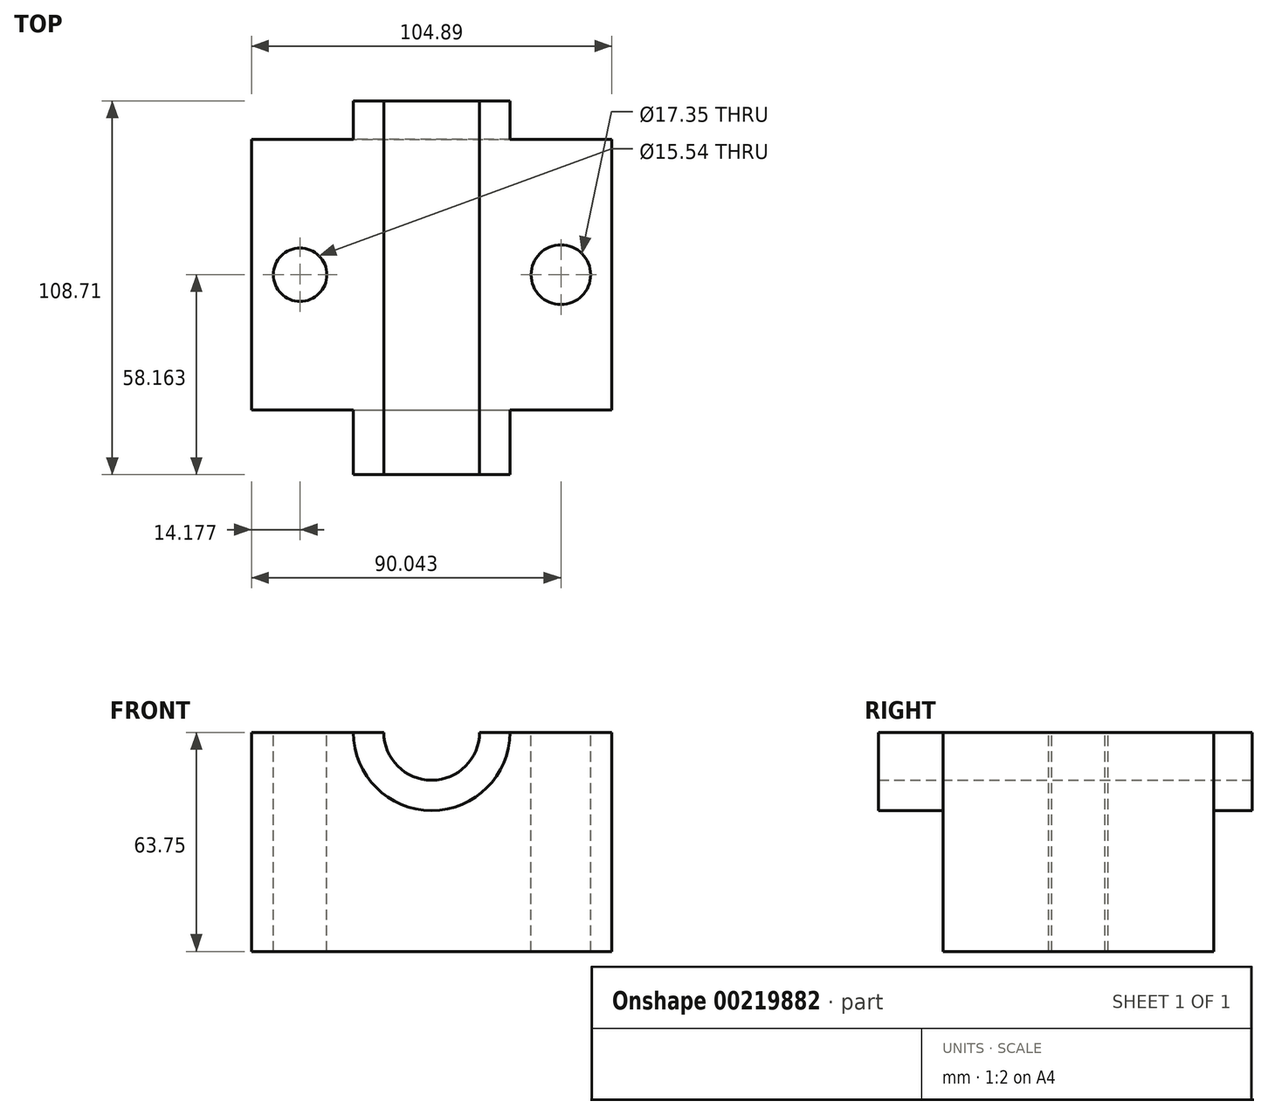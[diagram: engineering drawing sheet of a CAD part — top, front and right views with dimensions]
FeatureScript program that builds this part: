
annotation { "Feature Type Name" : "Feature", "Feature Type Description" : "" }
export const myFeature = defineFeature(function(context is Context, id is Id, definition is map)
    precondition{}
    {
        {
            var Q0;
            Q0=qCreatedBy(makeId("Top.planeOp"),FACE);
            var sketch = newSketch(context, id + "F0", { "sketchPlane" : qUnion([Q0])});
            skLineSegment(sketch, "E0.bottom", {"start": v(-48.1, -18.27) * mm, "end": v(56.79, -18.27) * mm});
            skLineSegment(sketch, "E0.top", {"start": v(-48.1, 60.46) * mm, "end": v(56.79, 60.46) * mm});
            skLineSegment(sketch, "E0.left", {"start": v(-48.1, -18.27) * mm, "end": v(-48.1, 60.46) * mm});
            skLineSegment(sketch, "E0.right", {"start": v(56.79, -18.27) * mm, "end": v(56.79, 60.46) * mm});
            skSolve(sketch);
        }
        {
            var Q0;
            Q0 = qSketchRegion(id + "F0", true);
            extrude(context, id + "F1", {"entities" : qUnion([Q0]), "depth" : 63.75 * mm});
        }
        {
            var Q0;
            Q0=makeQuery(id+"F1.opExtrude","SWEPT_FACE",FACE,{"disambiguationData":[OSD([sQuery(id+"F0.wireOp",EDGE,"E0.bottom")])]});
            var sketch = newSketch(context, id + "F2", { "sketchPlane" : qUnion([Q0])});
            skLineSegment(sketch, "E1", {"start": v(-48.1, 63.75) * mm, "end": v(56.79, 63.75) * mm});
            skCircle(sketch, "E2", {"center": v(4.34, 63.75) * mm, "radius": 22.76 * mm});
            skCircle(sketch, "E3", {"center": v(4.34, 63.75) * mm, "radius": 13.93 * mm});
            skLineSegment(sketch, "E4", {"start": v(-18.42, 63.75) * mm, "end": v(27.1, 63.75) * mm});
            skSolve(sketch);
        }
        {
            var Q0;
            {var subQ0=sQuery(id+"F2.wireOp",EDGE,"E4");var subQ5=sQuery(id+"F2.wireOp",EDGE,"E3");var subQ7=makeQuery(id+"F2.imprint","INTERSECT",VERTEX,{"disambiguationData":[OD(0.0)],"derivedFrom":[subQ5,subQ0]});Q0=makeQuery(id+"F2.imprint","IMPRINT",FACE,{"disambiguationData":[TD([[makeQuery(id+"F2.imprint","IMPRINT",EDGE,{"disambiguationData":[TD([[subQ7,-1.0]])],"derivedFrom":subQ5}),-1.0]])]});}
            extrude(context, id + "F3", {"entities" : qUnion([Q0]), "operationType" : NewBodyOperationType.ADD, "depth" : 18.8 * mm});
        }
        {
            var Q0;
            {var subQ0=sQuery(id+"F0.wireOp",EDGE,"E0.bottom");var subQ1=sQuery(id+"F2.wireOp",EDGE,"E3");Q0=makeQuery(id+"F3.boolean.opBoolean","SPLIT",FACE,{"disambiguationData":[TD([makeQuery(id+"F3.opExtrude","SWEPT_FACE",FACE,{"disambiguationData":[OSD([subQ1])]})])],"derivedFrom":makeQuery(id+"F1.opExtrude","SWEPT_FACE",FACE,{"disambiguationData":[OSD([subQ0])]})});}
            extrude(context, id + "F4", {"entities" : qUnion([Q0]), "operationType" : NewBodyOperationType.REMOVE, "oppositeDirection" : true, "depth" : 105.16 * mm});
        }
        {
            var Q0;
            Q0=makeQuery(id+"F3.opExtrude","CAP_FACE",FACE,{"disambiguationData":[OSD([sQuery(id+"F2.wireOp",EDGE,"E2"),sQuery(id+"F2.wireOp",EDGE,"E3"),sQuery(id+"F2.wireOp",EDGE,"E4")])],"isStart":false});
            extrude(context, id + "F5", {"entities" : qUnion([Q0]), "operationType" : NewBodyOperationType.ADD, "oppositeDirection" : true, "depth" : 108.7 * mm});
        }
        {
            var Q0;
            {var subQ0=sQuery(id+"F2.wireOp",EDGE,"E4");var subQ3=sQuery(id+"F2.wireOp",EDGE,"E3");var subQ4=makeQuery(id+"F2.imprint","IMPRINT",EDGE,{"disambiguationData":[TD([[makeQuery(id+"F2.imprint","INTERSECT",VERTEX,{"disambiguationData":[OD(1.0)],"derivedFrom":[subQ3,subQ0]}),-1.0]])],"derivedFrom":subQ0});var subQ5=sQuery(id+"F0.wireOp",EDGE,"E0.right");var subQ6=sQuery(id+"F0.wireOp",EDGE,"E0.top");var subQ7=sQuery(id+"F0.wireOp",EDGE,"E0.bottom");Q0=makeQuery(id+"F5.boolean.opBoolean","MERGE",FACE,{"derivedFrom":[makeQuery(id+"F4.boolean.opBoolean","SPLIT",FACE,{"disambiguationData":[TD([makeQuery(id+"F1.opExtrude","SWEPT_FACE",FACE,{"disambiguationData":[OSD([subQ5])]})])],"derivedFrom":makeQuery(id+"F3.boolean.opBoolean","MERGE",FACE,{"derivedFrom":[makeQuery(id+"F1.opExtrude","CAP_FACE",FACE,{"disambiguationData":[OSD([subQ7,subQ6,sQuery(id+"F0.wireOp",EDGE,"E0.left"),subQ5])],"isStart":false}),makeQuery(id+"F3.opExtrude","SWEPT_FACE",FACE,{"disambiguationData":[OSD([subQ0]),TDD([makeQuery(id+"F2.imprint","IMPRINT",EDGE,{"disambiguationData":[TD([[makeQuery(id+"F2.imprint","INTERSECT",VERTEX,{"disambiguationData":[OD(0.0)],"derivedFrom":[subQ3,subQ0]}),1.0]])],"derivedFrom":subQ0})])]}),makeQuery(id+"F3.opExtrude","SWEPT_FACE",FACE,{"disambiguationData":[OSD([subQ0]),TDD([subQ4])]})]})}),makeQuery(id+"F5.opExtrude","SWEPT_FACE",FACE,{"disambiguationData":[OSD([subQ0]),TDD([makeQuery(id+"F3.opExtrude","CAP_EDGE",EDGE,{"disambiguationData":[OSD([subQ0]),TDD([subQ4])],"isStart":false})])]})]});}
            var sketch = newSketch(context, id + "F6", { "sketchPlane" : qUnion([Q0])});
            skLineSegment(sketch, "E5", {"start": v(27.1, 60.46) * mm, "end": v(56.79, 60.46) * mm});
            skLineSegment(sketch, "E6", {"start": v(27.1, -18.27) * mm, "end": v(-48.77, -18.27) * mm});
            skLineSegment(sketch, "E7", {"start": v(-19.08, 60.46) * mm, "end": v(-50.42, 60.46) * mm});
            skPoint(sketch, "E8.centerSnap0", {"position": v(-33.92, 21.1) * mm});
            skLineSegment(sketch, "E9", {"start": v(-48.77, -18.27) * mm, "end": v(-18.66, -18.27) * mm});
            skCircle(sketch, "E10", {"center": v(41.94, 21.1) * mm, "radius": 8.68 * mm});
            skCircle(sketch, "E11", {"center": v(-33.92, 21.1) * mm, "radius": 7.77 * mm});
            skSolve(sketch);
        }
        {
            var Q0;
            Q0=makeQuery(id+"F6.imprint","IMPRINT",FACE,{"disambiguationData":[TD([[makeQuery(id+"F6.imprint","IMPRINT",EDGE,{"derivedFrom":sQuery(id+"F6.wireOp",EDGE,"E11")}),1.0]])]});
            var Q1;
            Q1=makeQuery(id+"F6.imprint","IMPRINT",FACE,{"disambiguationData":[TD([[makeQuery(id+"F6.imprint","IMPRINT",EDGE,{"derivedFrom":sQuery(id+"F6.wireOp",EDGE,"E10")}),1.0]])]});
            extrude(context, id + "F7", {"entities" : qUnion([Q0, Q1]), "operationType" : NewBodyOperationType.REMOVE, "oppositeDirection" : true, "depth" : 90.17 * mm});
        }
    });
